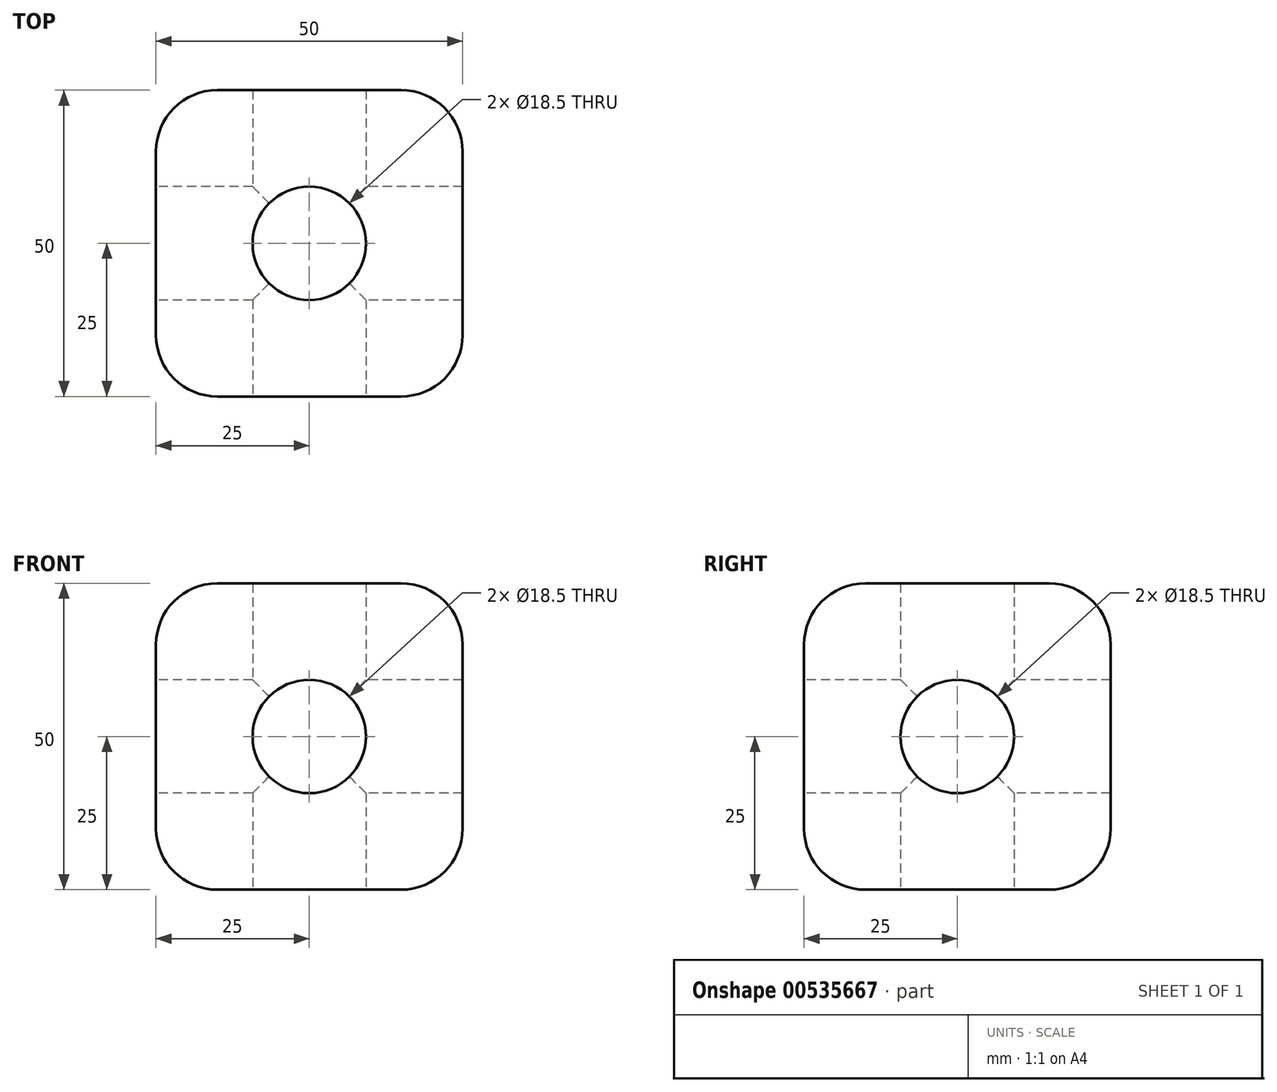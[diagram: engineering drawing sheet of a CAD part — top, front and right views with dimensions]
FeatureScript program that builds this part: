
annotation { "Feature Type Name" : "Feature", "Feature Type Description" : "" }
export const myFeature = defineFeature(function(context is Context, id is Id, definition is map)
    precondition{}
    {
        {
            var Q0;
            Q0=qCreatedBy(makeId("Front.planeOp"),FACE);
            var sketch = newSketch(context, id + "F0", { "sketchPlane" : qUnion([Q0])});
            skLineSegment(sketch, "E0.bottom", {"start": v(25, -25) * mm, "end": v(-25, -25) * mm});
            skLineSegment(sketch, "E0.top", {"start": v(25, 25) * mm, "end": v(-25, 25) * mm});
            skLineSegment(sketch, "E0.left", {"start": v(25, -25) * mm, "end": v(25, 25) * mm});
            skLineSegment(sketch, "E0.right", {"start": v(-25, -25) * mm, "end": v(-25, 25) * mm});
            skPoint(sketch, "E0.middle", {"position": v(0, 0) * mm});
            skSolve(sketch);
        }
        {
            var Q0;
            Q0 = qSketchRegion(id + "F0", true);
            extrude(context, id + "F1", {"entities" : qUnion([Q0]), "depth" : 50 * mm, "offsetDistance" : 25 * mm});
        }
        {
            var Q0;
            Q0=makeQuery(id+"F1.opExtrude","CAP_FACE",FACE,{"disambiguationData":[OSD([sQuery(id+"F0.wireOp",EDGE,"E0.bottom"),sQuery(id+"F0.wireOp",EDGE,"E0.top"),sQuery(id+"F0.wireOp",EDGE,"E0.left"),sQuery(id+"F0.wireOp",EDGE,"E0.right")])],"isStart":false});
            var sketch = newSketch(context, id + "F2", { "sketchPlane" : qUnion([Q0])});
            skCircle(sketch, "E1", {"center": v(0, 0) * mm, "radius": 9.25 * mm});
            skSolve(sketch);
        }
        {
            var Q0;
            Q0 = qSketchRegion(id + "F2", true);
            var Q1;
            Q1=makeQuery(id+"F1.opExtrude","CAP_FACE",FACE,{"disambiguationData":[OSD([sQuery(id+"F0.wireOp",EDGE,"E0.bottom"),sQuery(id+"F0.wireOp",EDGE,"E0.top"),sQuery(id+"F0.wireOp",EDGE,"E0.left"),sQuery(id+"F0.wireOp",EDGE,"E0.right")])],"isStart":true});
            extrude(context, id + "F3", {"entities" : qUnion([Q0]), "operationType" : NewBodyOperationType.REMOVE, "endBound" : BoundingType.UP_TO_SURFACE, "oppositeDirection" : true, "depth" : 43 * mm, "endBoundEntityFace" : qUnion([Q1]), "offsetDistance" : 25 * mm});
        }
        {
            var Q0;
            Q0=makeQuery(id+"F1.opExtrude","SWEPT_FACE",FACE,{"disambiguationData":[OSD([sQuery(id+"F0.wireOp",EDGE,"E0.right")])]});
            var sketch = newSketch(context, id + "F4", { "sketchPlane" : qUnion([Q0])});
            skLineSegment(sketch, "E2", {"start": v(25, 25) * mm, "end": v(25, -25) * mm, "construction": true});
            skLineSegment(sketch, "E3", {"start": v(50, 0) * mm, "end": v(0, 0) * mm, "construction": true});
            skCircle(sketch, "E4", {"center": v(25, 0) * mm, "radius": 9.25 * mm});
            skSolve(sketch);
        }
        {
            var Q0;
            Q0 = qSketchRegion(id + "F4", true);
            var Q1;
            Q1=makeQuery(id+"F1.opExtrude","SWEPT_FACE",FACE,{"disambiguationData":[OSD([sQuery(id+"F0.wireOp",EDGE,"E0.left")])]});
            extrude(context, id + "F5", {"entities" : qUnion([Q0]), "operationType" : NewBodyOperationType.REMOVE, "endBound" : BoundingType.UP_TO_SURFACE, "oppositeDirection" : true, "depth" : 43 * mm, "endBoundEntityFace" : qUnion([Q1]), "offsetDistance" : 25 * mm});
        }
        {
            var Q0;
            Q0=makeQuery(id+"F1.opExtrude","SWEPT_FACE",FACE,{"disambiguationData":[OSD([sQuery(id+"F0.wireOp",EDGE,"E0.bottom")])]});
            var sketch = newSketch(context, id + "F6", { "sketchPlane" : qUnion([Q0])});
            skLineSegment(sketch, "E5", {"start": v(0, 50) * mm, "end": v(0, 0) * mm, "construction": true});
            skLineSegment(sketch, "E6", {"start": v(25, 25) * mm, "end": v(-25, 25) * mm, "construction": true});
            skCircle(sketch, "E7", {"center": v(0, 25) * mm, "radius": 9.25 * mm});
            skSolve(sketch);
        }
        {
            var Q0;
            Q0 = qSketchRegion(id + "F6", true);
            var Q1;
            Q1=makeQuery(id+"F1.opExtrude","SWEPT_FACE",FACE,{"disambiguationData":[OSD([sQuery(id+"F0.wireOp",EDGE,"E0.top")])]});
            extrude(context, id + "F7", {"entities" : qUnion([Q0]), "operationType" : NewBodyOperationType.REMOVE, "endBound" : BoundingType.UP_TO_SURFACE, "oppositeDirection" : true, "depth" : 43 * mm, "endBoundEntityFace" : qUnion([Q1]), "offsetDistance" : 25 * mm});
        }
        {
            var Q0;
            Q0=makeQuery(id+"F1.opExtrude","CAP_EDGE",EDGE,{"disambiguationData":[OSD([sQuery(id+"F0.wireOp",EDGE,"E0.bottom")])],"isStart":false});
            var Q1;
            Q1=makeQuery(id+"F1.opExtrude","CAP_EDGE",EDGE,{"disambiguationData":[OSD([sQuery(id+"F0.wireOp",EDGE,"E0.top")])],"isStart":false});
            var Q2;
            Q2=makeQuery(id+"F1.opExtrude","CAP_EDGE",EDGE,{"disambiguationData":[OSD([sQuery(id+"F0.wireOp",EDGE,"E0.top")])],"isStart":true});
            var Q3;
            Q3=makeQuery(id+"F1.opExtrude","CAP_EDGE",EDGE,{"disambiguationData":[OSD([sQuery(id+"F0.wireOp",EDGE,"E0.bottom")])],"isStart":true});
            var Q4;
            Q4=makeQuery(id+"F1.opExtrude","SWEPT_EDGE",EDGE,{"disambiguationData":[OSD([sQuery(id+"F0.wireOp",EDGE,"E0.bottom"),sQuery(id+"F0.wireOp",EDGE,"E0.left")])]});
            var Q5;
            Q5=makeQuery(id+"F1.opExtrude","SWEPT_EDGE",EDGE,{"disambiguationData":[OSD([sQuery(id+"F0.wireOp",EDGE,"E0.top"),sQuery(id+"F0.wireOp",EDGE,"E0.left")])]});
            var Q6;
            Q6=makeQuery(id+"F1.opExtrude","CAP_EDGE",EDGE,{"disambiguationData":[OSD([sQuery(id+"F0.wireOp",EDGE,"E0.left")])],"isStart":true});
            var Q7;
            Q7=makeQuery(id+"F1.opExtrude","CAP_EDGE",EDGE,{"disambiguationData":[OSD([sQuery(id+"F0.wireOp",EDGE,"E0.left")])],"isStart":false});
            var Q8;
            Q8=makeQuery(id+"F1.opExtrude","CAP_EDGE",EDGE,{"disambiguationData":[OSD([sQuery(id+"F0.wireOp",EDGE,"E0.right")])],"isStart":true});
            var Q9;
            Q9=makeQuery(id+"F1.opExtrude","CAP_EDGE",EDGE,{"disambiguationData":[OSD([sQuery(id+"F0.wireOp",EDGE,"E0.right")])],"isStart":false});
            var Q10;
            Q10=makeQuery(id+"F1.opExtrude","SWEPT_EDGE",EDGE,{"disambiguationData":[OSD([sQuery(id+"F0.wireOp",EDGE,"E0.bottom"),sQuery(id+"F0.wireOp",EDGE,"E0.right")])]});
            var Q11;
            Q11=makeQuery(id+"F1.opExtrude","SWEPT_EDGE",EDGE,{"disambiguationData":[OSD([sQuery(id+"F0.wireOp",EDGE,"E0.top"),sQuery(id+"F0.wireOp",EDGE,"E0.right")])]});
            fillet(context, id + "F8", {"entities" : qUnion([Q0, Q1, Q2, Q3, Q4, Q5, Q6, Q7, Q8, Q9, Q10, Q11]), "radius" : 10 * mm, "tangentPropagation" : true, "allowEdgeOverflow" : false});
        }
    });
